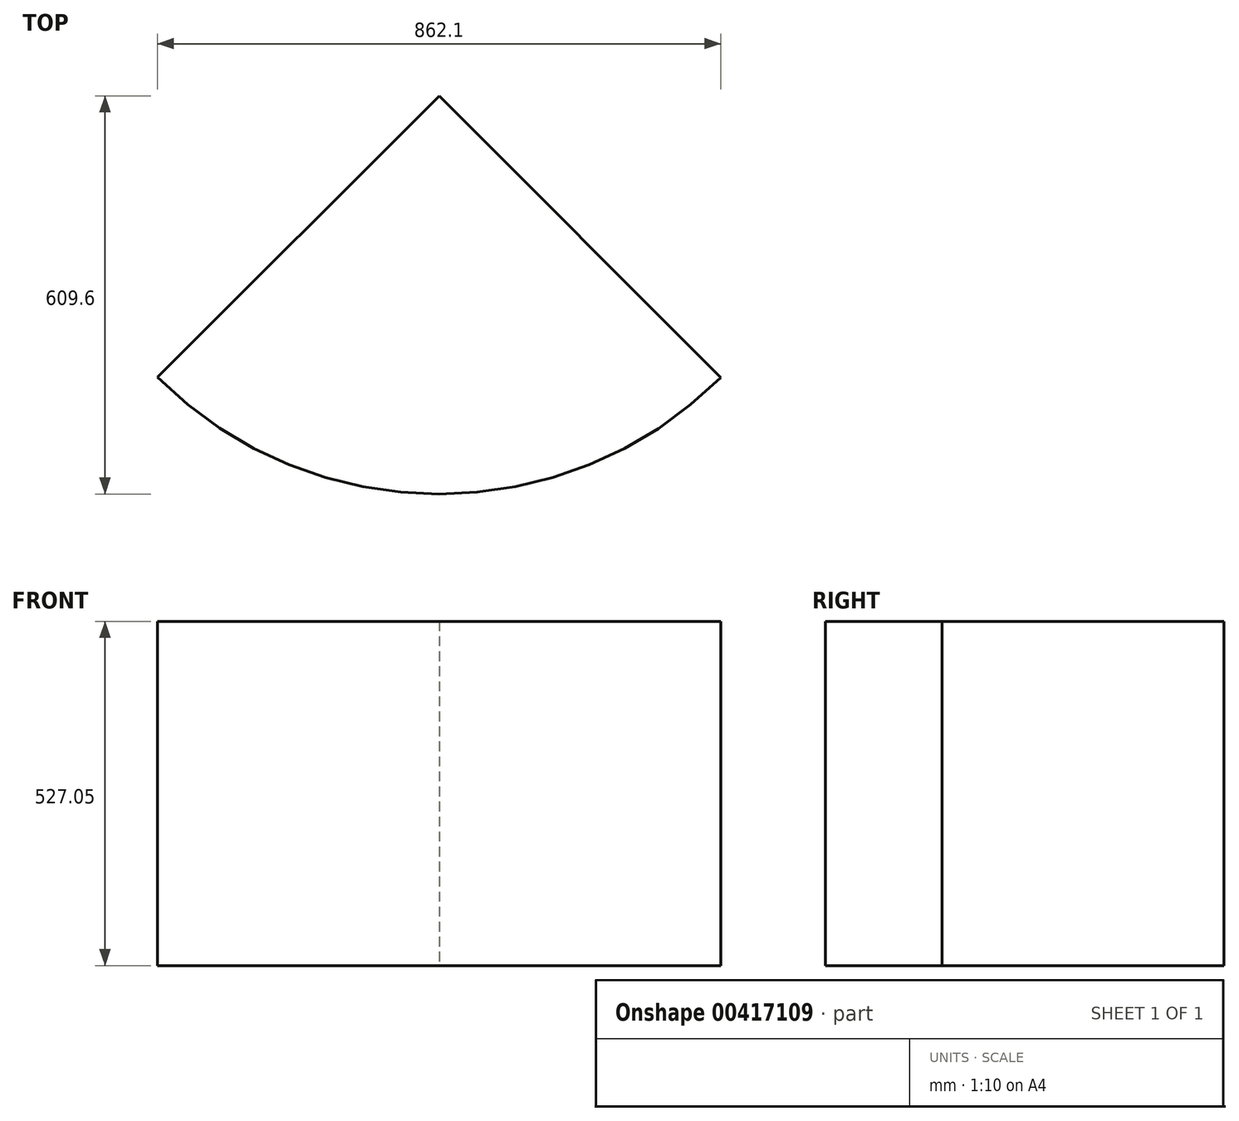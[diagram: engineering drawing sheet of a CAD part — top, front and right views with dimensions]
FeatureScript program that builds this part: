
annotation { "Feature Type Name" : "Feature", "Feature Type Description" : "" }
export const myFeature = defineFeature(function(context is Context, id is Id, definition is map)
    precondition{}
    {
        {
            var Q0;
            Q0=qCreatedBy(makeId("Top.planeOp"),FACE);
            var sketch = newSketch(context, id + "F0", { "sketchPlane" : qUnion([Q0])});
            skLineSegment(sketch, "E0", {"start": v(0, 0) * mm, "end": v(-431.2, -430.91) * mm});
            skLineSegment(sketch, "E1", {"start": v(0, 0) * mm, "end": v(430.91, -431.2) * mm});
            skArc(sketch, "E2", {"start": v(-431.2, -430.91) * mm, "mid": v(-0.2, -609.6) * mm, "end": v(430.91, -431.2) * mm});
            skSolve(sketch);
        }
        {
            var Q0;
            Q0=makeQuery(id+"F0.imprint","IMPRINT",FACE,{"disambiguationData":[TD([[makeQuery(id+"F0.imprint","IMPRINT",EDGE,{"derivedFrom":sQuery(id+"F0.wireOp",EDGE,"E0")}),1.0]])]});
            extrude(context, id + "F1", {"entities" : qUnion([Q0]), "depth" : 527.05 * mm});
        }
    });
